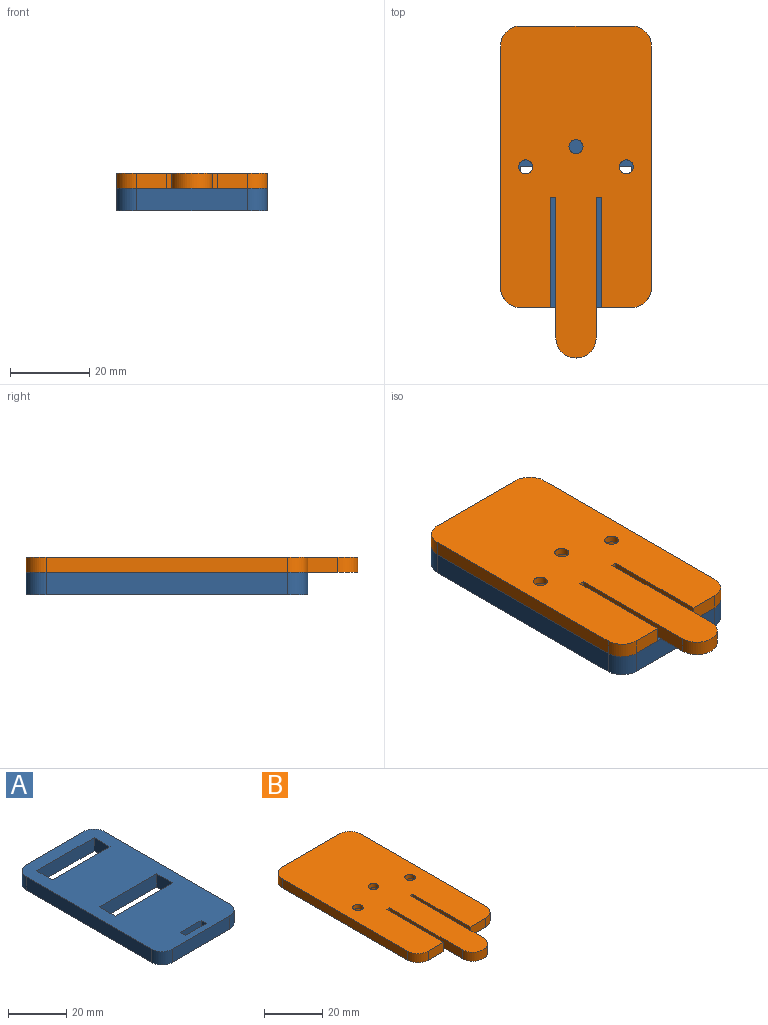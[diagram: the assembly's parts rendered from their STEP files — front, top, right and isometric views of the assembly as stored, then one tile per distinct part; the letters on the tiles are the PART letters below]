
ASSEMBLY  parts=2 mates=1
PART A: 27 faces, bbox 38.1x71.1x5.6 mm
  f0: plane 27.94x5.21mm, normal (0,0,-1), area 145.5mm2, adj f8,f9,f10,f20
  f1: plane 27.94x5.21mm, normal (0,0,-1), area 145.5mm2, adj f12,f13,f14,f21
  f2: plane 71.12x38.1mm, normal (0,0,1), area 2228.8mm2, adj f3,f4,f5,f6,f7,f8,f9,f10
  f3: plane 27.94x5.59mm, normal (0,1,0), area 156.1mm2, adj f2,f19,f23,f26
  f4: plane 60.96x5.59mm, normal (-1,0,0), area 340.6mm2, adj f2,f19,f23,f24
  f5: plane 27.94x5.59mm, normal (0,-1,0), area 156.1mm2, adj f2,f19,f24,f25
  f6: plane 60.96x5.59mm, normal (1,0,0), area 340.6mm2, adj f2,f19,f25,f26
  f7: plane 27.94x5.59mm, normal (0,-1,0), area 156.1mm2, adj f2,f8,f10,f19
  f8: plane 12.95x5.59mm, normal (1,0,0), area 59.2mm2, adj f0,f2,f7,f9,f19,f20
  f9: plane 27.94x2.54mm, normal (0,1,0), area 71mm2, adj f0,f2,f8,f10
  f10: plane 12.95x5.59mm, normal (-1,0,0), area 59.2mm2, adj f0,f2,f7,f9,f19,f20
  f11: plane 27.94x5.59mm, normal (0,-1,0), area 156.1mm2, adj f2,f12,f14,f19
  f12: plane 12.95x5.59mm, normal (1,0,0), area 59.2mm2, adj f1,f2,f11,f13,f19,f21
  f13: plane 27.94x2.54mm, normal (0,1,0), area 71mm2, adj f1,f2,f12,f14
  f14: plane 12.95x5.59mm, normal (-1,0,0), area 59.2mm2, adj f1,f2,f11,f13,f19,f21
  f15: plane 10.16x2.54mm, normal (0,1,0), area 25.8mm2, adj f2,f16,f18,f22
  f16: plane 2.54x2.54mm, normal (1,0,0), area 6.5mm2, adj f2,f15,f17,f22
  f17: plane 10.16x2.54mm, normal (0,-1,0), area 25.8mm2, adj f2,f16,f18,f22
  f18: plane 2.54x2.54mm, normal (-1,0,0), area 6.5mm2, adj f2,f15,f17,f22
  f19: plane 71.12x38.1mm, normal (0,0,-1), area 1963.7mm2, adj f3,f4,f5,f6,f7,f8,f10,f11
  f20: plane 27.94x3.05mm, normal (0,1,0), area 85.2mm2, adj f0,f8,f10,f19
  f21: plane 27.94x3.05mm, normal (0,1,0), area 85.2mm2, adj f1,f12,f14,f19
  f22: plane 10.16x2.54mm, normal (0,0,1), area 25.8mm2, adj f15,f16,f17,f18
  f23: cylinder r=5.08mm len=5.59mm, axis (0,0,1), area 44.6mm2, adj f2,f3,f4,f19
  f24: cylinder r=5.08mm len=5.59mm, axis (0,0,-1), area 44.6mm2, adj f2,f4,f5,f19
  f25: cylinder r=5.08mm len=5.59mm, axis (0,0,1), area 44.6mm2, adj f2,f5,f6,f19
  f26: cylinder r=5.08mm len=5.59mm, axis (0,0,-1), area 44.6mm2, adj f2,f3,f6,f19
PART B: 44 faces, bbox 38.1x83.8x9.3 mm
  f0: plane 7.49x5.46mm, normal (-1,0,0), area 25.6mm2, adj f1,f3,f4,f5,f6,f7,f31
  f1: plane 26.67x1.27mm, normal (0,-1,0), area 33.9mm2, adj f0,f2,f4,f31
  f2: plane 7.49x5.46mm, normal (1,0,0), area 25.6mm2, adj f1,f3,f4,f5,f6,f7,f31
  f3: plane 26.67x3.68mm, normal (0,0,1), area 98.2mm2, adj f0,f2,f5,f31
  f4: plane 26.67x7.49mm, normal (0,0,-1), area 199.8mm2, adj f0,f1,f2,f6
  f5: plane 26.67x6.73mm, normal (0,-1,0), area 87.6mm2, adj f0,f2,f3,f7,f16,f17,f18,f19
  f6: plane 26.67x5.46mm, normal (0,1,0), area 145.6mm2, adj f0,f2,f4,f7
  f7: plane 71.12x38.1mm, normal (0,0,-1), area 2062mm2, adj f0,f2,f5,f6,f9,f11,f14,f15
  f8: plane 16.87x10.16mm, normal (0,0,-1), area 145.4mm2, adj f17,f18,f28,f29,f30,f37
  f9: plane 7.49x5.46mm, normal (-1,0,0), area 25.6mm2, adj f7,f10,f12,f13,f14,f15,f32
  f10: plane 26.67x1.27mm, normal (0,-1,0), area 33.9mm2, adj f9,f11,f13,f32
  f11: plane 7.49x5.46mm, normal (1,0,0), area 25.6mm2, adj f7,f10,f12,f13,f14,f15,f32
  f12: plane 26.67x3.68mm, normal (0,0,1), area 98.2mm2, adj f9,f11,f14,f32
  f13: plane 26.67x7.49mm, normal (0,0,-1), area 199.8mm2, adj f9,f10,f11,f15
  f14: plane 26.67x2.92mm, normal (0,-1,0), area 77.9mm2, adj f7,f9,f11,f12
  f15: plane 26.67x5.46mm, normal (0,1,0), area 145.6mm2, adj f7,f9,f11,f13
  f16: plane 27.81x3.81mm, normal (1,0,0), area 106mm2, adj f5,f7,f24,f25
  f17: plane 35.43x4.54mm, normal (-1,0,0), area 135.3mm2, adj f5,f8,f25,f26,f27,f29,f37
  f18: plane 35.43x4.54mm, normal (1,0,0), area 135.3mm2, adj f5,f8,f25,f26,f27,f30,f37
  f19: plane 27.81x3.81mm, normal (-1,0,0), area 106mm2, adj f5,f7,f20,f25
  f20: plane 7.62x3.81mm, normal (0,-1,0), area 29mm2, adj f7,f19,f25,f33
  f21: plane 60.96x3.81mm, normal (1,0,0), area 232.3mm2, adj f7,f25,f33,f34
  f22: plane 27.94x3.81mm, normal (0,1,0), area 106.5mm2, adj f7,f25,f34,f35
  f23: plane 60.96x3.81mm, normal (-1,0,0), area 232.3mm2, adj f7,f25,f35,f36
  f24: plane 7.62x3.81mm, normal (0,-1,0), area 29mm2, adj f7,f16,f25,f36
  f25: plane 83.82x38.1mm, normal (0,0,1), area 2705mm2, adj f5,f16,f17,f18,f19,f20,f21,f22
  f26: plane 22.73x10.16mm, normal (0,0,-1), area 231mm2, adj f5,f17,f18,f27
  f27: plane 10.16x2.03mm, normal (0,1,0), area 19.3mm2, adj f17,f18,f26,f28,f29,f30
  f28: plane 8.13x2.54mm, normal (0,-0.62,-0.78), area 26.4mm2, adj f8,f27,f29,f30
  f29: plane 2.54x2.03mm, normal (-0.71,-0.44,-0.55), area 3.2mm2, adj f8,f17,f27,f28
  f30: plane 2.54x2.03mm, normal (0.71,-0.44,-0.55), area 3.2mm2, adj f8,f18,f27,f28
  f31: plane 26.67x1.27mm, normal (0,-0.71,0.71), area 47.9mm2, adj f0,f1,f2,f3
  f32: plane 26.67x1.27mm, normal (0,-0.71,0.71), area 47.9mm2, adj f9,f10,f11,f12
  f33: cylinder r=5.08mm len=5.08mm, axis (0,0,1), area 30.4mm2, adj f7,f20,f21,f25
  f34: cylinder r=5.08mm len=5.08mm, axis (0,0,-1), area 30.4mm2, adj f7,f21,f22,f25
  f35: cylinder r=5.08mm len=5.08mm, axis (0,0,1), area 30.4mm2, adj f7,f22,f23,f25
  f36: cylinder r=5.08mm len=5.08mm, axis (0,0,-1), area 30.4mm2, adj f7,f23,f24,f25
  f37: cylinder r=5.08mm len=10.16mm, axis (0,0,1), area 60.8mm2, adj f8,f17,f18,f25
  f38: cylinder r=1.78mm len=3.56mm, axis (0,0,-1), area 19.9mm2, adj f25,f39
  f39: cone r=1.78mm half-angle=45deg, axis (0,0,-1), area 50.4mm2, adj f7,f38
  f40: cylinder r=1.78mm len=3.56mm, axis (0,0,-1), area 19.9mm2, adj f25,f41
  f41: cone r=1.78mm half-angle=45deg, axis (0,0,-1), area 50.4mm2, adj f7,f40
  f42: cylinder r=1.78mm len=3.56mm, axis (0,0,-1), area 19.9mm2, adj f25,f43
  f43: cone r=1.78mm half-angle=45deg, axis (0,0,-1), area 50.4mm2, adj f7,f42
PLACE A at identity
PLACE B t=(0,0,-5.46)mm
MATE fastened B.f7 <-> A.f2  axis (0,0,-1) through (38.1,-66.04,2.54)mm
